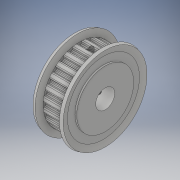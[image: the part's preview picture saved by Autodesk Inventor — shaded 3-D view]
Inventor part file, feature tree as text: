
AUTODESK INVENTOR PART (.ipt)
format: ipt  version: 2019 (Build 230136000, 136)  size: 538,624 bytes
history: native  units: mm
features: other x14, revolve x3, thread x2, hole x1, extrude x1, sketch x1
ambient origin geometry x8: Origin, YZ Plane, XZ Plane, XY Plane, X Axis, Y Axis, Z Axis, Center Point
bodies: Solid1 (feature_tree)
feature tree (22):
  revolve  "Revolution1"  [1 undecoded]
  hole  "Hole1"  [1 undecoded]
  extrude  "Extrusion1"  Depth=10.0mm TaperAngle=0.0deg
  revolve  "Revolution2"  Angle=360.0deg
  thread  "Thread1"  [1 undecoded]
  revolve  "Revolution3"  [1 undecoded]
  thread  "Thread2"  [1 undecoded]
  other  "to_screw1_XY"
  other  "to_screw1_YZ"
  other  "to_screw1_ZX"
  other  "to_screw1_X"
  other  "to_screw1_Y"
  other  "to_screw1_Z"
  other  "to_screw1_Center"
  other  "to_screw2_XY"
  other  "to_screw2_YZ"
  other  "to_screw2_ZX"
  other  "to_screw2_X"
  other  "to_screw2_Y"
  other  "to_screw2_Z"
  other  "to_screw2_Center"
  sketch  "Sketch2"  dims[d0=360.0deg d1=10.0mm d2=6.0mm d3=4.0mm d4=2.0mm d5=90.0deg d6=16.0mm d7=0.0mm d8=11.0mm d9=0.0mm d10=360.0deg d11=14.15mm d12=0.0mm d13=360.0deg d14=14.15mm d15=0.0mm]
note: 5 required parameter values undecoded (feature->parameter linkage not recoverable at this tier; creation-order binding heuristic only, values carry confidence <= 0.55)